# Revit family: Haworth_Pergola_Ceiling_Slat
name_source: partatom
category: Furniture Systems
revit_build: Autodesk Revit 2018 (Build: 20170223_1515(x64)
units: mm (PartAtom-declared; Revit-internal decimal feet)

## family parameters
Always vertical = Yes
Cut with Voids When Loaded = No
OmniClass Number = 23.40.70.14.64.21
OmniClass Title = Systems Furniture
Part Type = Normal
Room Calculation Point = No
Round Connector Dimension = Use Diameter
Shared = No
Work Plane-Based = No

## types (5) — shared parameters
Actual Height = 3.63 "
Actual Mounting Height = 92.37 "
Assembly Code = E2020200
Ceiling Slat Offset = 1 "
Ceiling Spacing = 6 "
Custom Size = No
Description = Haworth - Pergola Ceiling - Slat
Manufacturer = Haworth
Max. Depth = 144 "
Max. Height = 96 "
Max. Width = 144 "
Min. Depth = 48 "
Min. Height = 96 "
Min. Width = 48 "
Model = Haworth Pergola
Revision Number = 1
Size = Verify Final Dim. w/ Haworth
Standard Length = 48, 72, 96, 120, 144 in.
Sustainability Info = http://www.haworth.com
Top Trim Width = 0.5 "
Trim Finish = Haworth _ Paint _ Undecided _ Pergola
URL = http://www.haworth.com
URL - Product = https://www.haworth.com
Warranty = http://www.haworth.com

## per-type parameters (varying)
| type | Actual Depth | Actual Width | Depth | Slat Count | Width |
| 48d 48w | 48 " | 48 " | 48 " | 8 | 48 " |
| 72d 72w | 72 " | 72 " | 72 " | 12 | 72 " |
| 96d 96w | 96 " | 96 " | 96 " | 16 | 96 " |
| 120d 120w | 120 " | 120 " | 120 " | 20 | 120 " |
| 144d 144w | 144 " | 144 " | 144 " | 24 | 144 " |

## geometry (parser evidence)
native form markers: Sweep x6
no freeform markers — native parametric forms only
